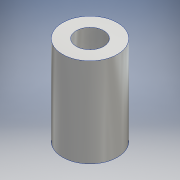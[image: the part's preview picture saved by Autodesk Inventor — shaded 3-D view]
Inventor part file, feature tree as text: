
AUTODESK INVENTOR PART (.ipt)
format: ipt  version: 2016 (Build 200138000, 138)  size: 104,448 bytes
history: native  units: mm
features: other x1, extrude x1, sketch x1
ambient origin geometry x8: Origin, YZ Plane, XZ Plane, XY Plane, X Axis, Y Axis, Z Axis, Center Point
bodies: Body1 (feature_tree)
feature tree (3):
  other  "ソリッド1"
  extrude  "押し出し1"  Depth=4.0mm
  sketch  "スケッチ1"
